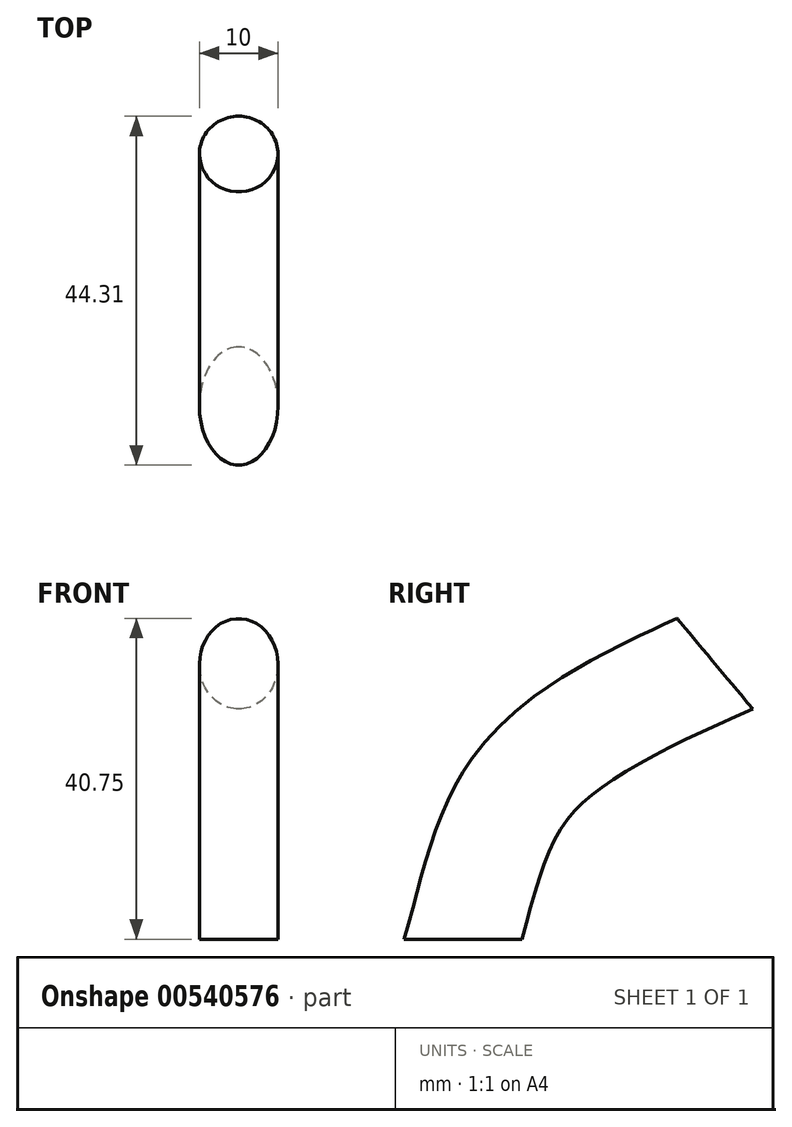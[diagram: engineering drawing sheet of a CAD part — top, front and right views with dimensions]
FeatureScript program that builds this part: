
annotation { "Feature Type Name" : "Feature", "Feature Type Description" : "" }
export const myFeature = defineFeature(function(context is Context, id is Id, definition is map)
    precondition{}
    {
        {
            var Q0;
            Q0=qCreatedBy(makeId("Right.planeOp"),FACE);
            var sketch = newSketch(context, id + "F0", { "sketchPlane" : qUnion([Q0])});
            skFitSpline(sketch, "E0", {"points": [v(0, 0) * mm, v(8, 20) * mm, v(32, 35) * mm], "startDerivative": vector(12.88, 45.07) * mm, "endDerivative": vector(50.56, 22.47) * mm});
            skSolve(sketch);
        }
        {
            var Q0;
            Q0=qCreatedBy(makeId("Top.planeOp"),FACE);
            var sketch = newSketch(context, id + "F1", { "sketchPlane" : qUnion([Q0])});
            skEllipse(sketch, "E1", {"center": v(0, 0) * mm, "majorRadius": 7.5 * mm, "minorRadius": 5 * mm, "majorAxis": v(0, 1)});
            skSolve(sketch);
        }
        {
            var Q0;
            Q0=makeQuery(id+"F1.imprint","IMPRINT",FACE,{"disambiguationData":[TD([[makeQuery(id+"F1.imprint","IMPRINT",EDGE,{"derivedFrom":sQuery(id+"F1.wireOp",EDGE,"E1")}),1.0]])]});
            var Q1;
            Q1=sQuery(id+"F0.wireOp",EDGE,"E0");
            sweep(context, id + "F2", {"profiles" : qUnion([Q0]), "path" : qUnion([Q1])});
        }
    });
